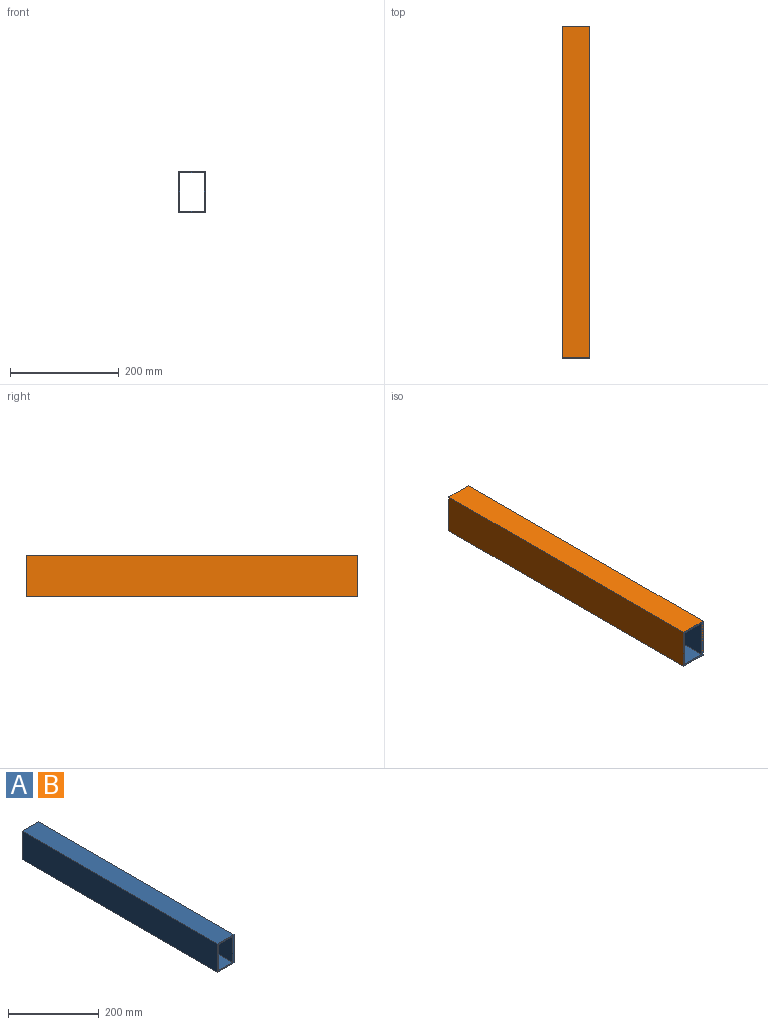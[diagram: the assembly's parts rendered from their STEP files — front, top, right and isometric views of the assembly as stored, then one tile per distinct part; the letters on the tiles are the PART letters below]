
ASSEMBLY  parts=2 mates=2
PART A: 10 faces, bbox 50.8x609.6x76.2 mm
  f0: plane 609.6x50.8mm, normal (0,0,1), area 30967.7mm2, adj f1,f7,f8,f9
  f1: plane 609.6x76.2mm, normal (-1,0,0), area 46451.5mm2, adj f0,f2,f8,f9
  f2: plane 609.6x50.8mm, normal (0,0,-1), area 30967.7mm2, adj f1,f7,f8,f9
  f3: plane 609.6x69.85mm, normal (-1,0,0), area 42580.6mm2, adj f4,f6,f8,f9
  f4: plane 609.6x44.45mm, normal (0,0,1), area 27096.7mm2, adj f3,f5,f8,f9
  f5: plane 609.6x69.85mm, normal (1,0,0), area 42580.6mm2, adj f4,f6,f8,f9
  f6: plane 609.6x44.45mm, normal (0,0,-1), area 27096.7mm2, adj f3,f5,f8,f9
  f7: plane 609.6x76.2mm, normal (1,0,0), area 46451.5mm2, adj f0,f2,f8,f9
  f8: plane 76.2x50.8mm, normal (0,-1,0), area 766.1mm2, adj f0,f1,f2,f3,f4,f5,f6,f7
  f9: plane 76.2x50.8mm, normal (0,1,0), area 766.1mm2, adj f0,f1,f2,f3,f4,f5,f6,f7
PART B: same geometry as A
PLACE A t=(-147.92,212.24,-69.26)mm
PLACE B t=(-147.92,212.24,-69.26)mm
MATE fastened B.f8 <-> A.f8  axis (0,-1,0) through (-122.52,-397.36,-31.16)mm
MATE parallel B.f7 <-> A.f1  axis (1,0,0) through (-97.12,-92.56,-31.16)mm
